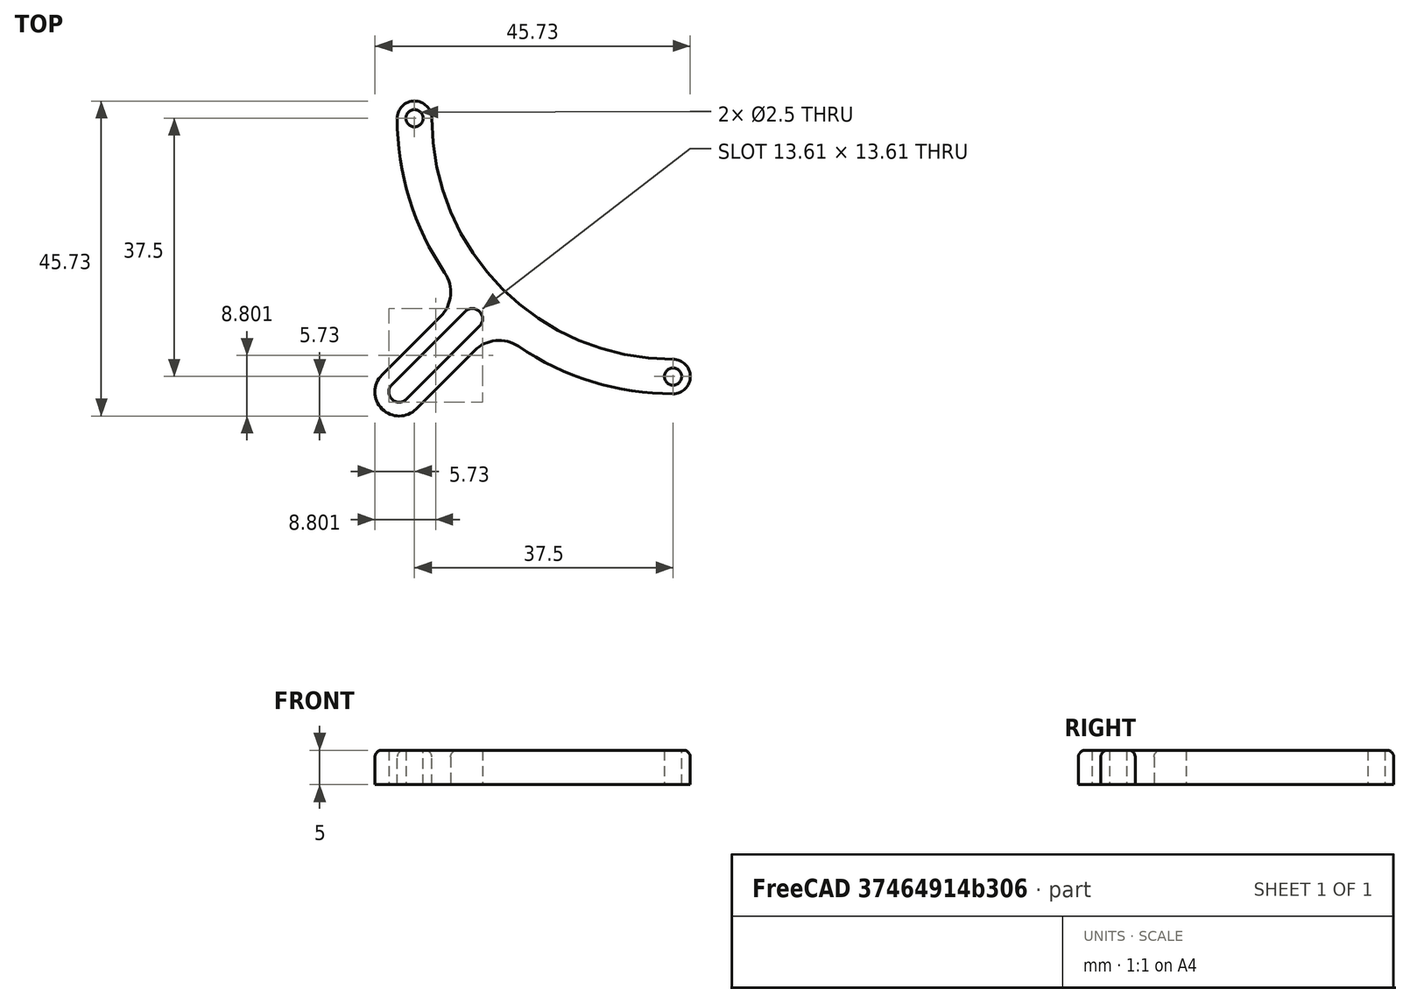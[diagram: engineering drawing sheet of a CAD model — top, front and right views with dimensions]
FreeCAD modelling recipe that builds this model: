
FCSTD DOCUMENT  (FreeCAD 2021.0205R23662 +3201 (Git))
Label: sketcher
License: All rights reserved
objects: Sketcher::SketchObject×1, PartDesign::Pad×1, PartDesign::Fillet×1, PartDesign::Body×1, App::Part×1, Mesh::Feature×1
note: 8 computed .brp shape members not serialized (recipe doc carries the construction recipe); baked Part::Feature solids carry a one-line shape summary decoded from their .brp

FEATURE [Sketcher::SketchObject] Sketch
  FullyConstrained = false
  MapMode = 5
  Support = -> [XY_Plane]
  sketch-geometry (17):
    g0: ArcOfCircle CenterX=0 CenterY=0 CenterZ=0 NormalX=0 NormalY=0 NormalZ=1 AngleXU=0 Radius=35 StartAngle=3.14159 EndAngle=4.71239
    g1: ArcOfCircle CenterX=0 CenterY=0 CenterZ=0 NormalX=0 NormalY=0 NormalZ=1 AngleXU=0 Radius=40 StartAngle=3.14159 EndAngle=3.73696
    g2: ArcOfCircle CenterX=-37.5 CenterY=0 CenterZ=0 NormalX=0 NormalY=0 NormalZ=1 AngleXU=0 Radius=2.5 StartAngle=0 EndAngle=3.14159
    g3: ArcOfCircle CenterX=0 CenterY=-37.5 CenterZ=0 NormalX=0 NormalY=0 NormalZ=1 AngleXU=0 Radius=2.5 StartAngle=4.71239 EndAngle=7.85398
    g4: Circle CenterX=-37.5 CenterY=0 CenterZ=0 NormalX=0 NormalY=0 NormalZ=1 AngleXU=0 Radius=1.25
    g5: Circle CenterX=0 CenterY=-37.5 CenterZ=0 NormalX=0 NormalY=0 NormalZ=1 AngleXU=0 Radius=1.25
    g6: LineSegment [constr] StartX=0 StartY=0 StartZ=0 EndX=-107.762 EndY=-107.762 EndZ=0
    g7: LineSegment StartX=-33.7219 StartY=-28.7721 StartZ=0 EndX=-42.2072 EndY=-37.2574 EndZ=0
    g8: ArcOfCircle CenterX=-39.7323 CenterY=-39.7323 CenterZ=0 NormalX=0 NormalY=0 NormalZ=1 AngleXU=0 Radius=3.5 StartAngle=2.35619 EndAngle=5.49779
    g9: LineSegment StartX=-37.2574 StartY=-42.2072 StartZ=0 EndX=-28.7721 EndY=-33.7219 EndZ=0
    g10: ArcOfCircle CenterX=0 CenterY=0 CenterZ=0 NormalX=0 NormalY=0 NormalZ=1 AngleXU=0 Radius=40 StartAngle=4.11702 EndAngle=4.71239
    g11: ArcOfCircle CenterX=-37.2574 CenterY=-25.2366 CenterZ=0 NormalX=0 NormalY=0 NormalZ=1 AngleXU=0 Radius=5 StartAngle=5.49779 EndAngle=6.87855
    g12: ArcOfCircle CenterX=-25.2366 CenterY=-37.2574 CenterZ=0 NormalX=0 NormalY=0 NormalZ=1 AngleXU=0 Radius=5 StartAngle=0.975429 EndAngle=2.35619
    g13: ArcOfCircle CenterX=-39.7323 CenterY=-39.7323 CenterZ=0 NormalX=0 NormalY=0 NormalZ=1 AngleXU=0 Radius=1.5 StartAngle=2.35619 EndAngle=5.49779
    g14: ArcOfCircle CenterX=-29.1257 CenterY=-29.1257 CenterZ=0 NormalX=0 NormalY=0 NormalZ=1 AngleXU=0 Radius=1.5 StartAngle=5.49779 EndAngle=8.63938
    g15: LineSegment StartX=-38.6716 StartY=-40.7929 StartZ=0 EndX=-28.065 EndY=-30.1863 EndZ=0
    g16: LineSegment StartX=-40.7929 StartY=-38.6716 StartZ=0 EndX=-30.1863 EndY=-28.065 EndZ=0
  constraints (44):
    c: Coincident(g0,g-1)
    c: PointOnObject(g0,g-1)
    c: PointOnObject(g0,g-2)
    c: Radius(g0) = 35
    c: Coincident(g1,g0)
    c: PointOnObject(g1,g-1)
    c: PointOnObject(g10,g-2)
    c: Radius(g1) = 40
    c: Coincident(g2,g1)
    c: Coincident(g2,g0)
    c: PointOnObject(g2,g-1)
    c: Coincident(g3,g0)
    c: Coincident(g3,g10)
    c: PointOnObject(g3,g-2)
    c: Coincident(g4,g2)
    c: Coincident(g5,g3)
    c: Equal(g4,g5)
    c: Diameter(g5) = 2.5
    c: Coincident(g6,g0)
    c: Angle(g-2,g6) = 2.35619
    c: Tangent(g7,g8) = -1.5708
    c: Tangent(g8,g9) = -1.5708
    c: Parallel(g7,g9)
    c: Parallel(g6,g9)
    c: Equal(g1,g10)
    c: Coincident(g1,g10)
    c: Tangent(g1,g11) = 1.5708
    c: Tangent(g7,g11) = 1.5708
    c: Tangent(g9,g12) = 1.5708
    c: Tangent(g10,g12) = 1.5708
    c: Equal(g11,g12)
    c: Radius(g11) = 5
    c: Diameter(g8) = 7
    c: PointOnObject(g8,g6)
    c: Distance(g8,g9) = 12
    c: Tangent(g13,g16) = 1.5708
    c: Tangent(g13,g15) = -1.5708
    c: Tangent(g15,g14) = -1.5708
    c: Tangent(g16,g14) = 1.5708
    c: Equal(g13,g14)
    c: Coincident(g13,g8)
    c: PointOnObject(g14,g6)
    c: Diameter(g14) = 3
    c: Distance(g15) = 15
FEATURE [PartDesign::Pad] Pad
  ClaimChildren = false
  Direction = (1,1,1)
  Fit = 0
  FitJoin = 0
  InnerFit = 0
  InnerFitJoin = 0
  InnerTaperAngle = 0
  InnerTaperAngleRev = 0
  Length = 5
  Length2 = 100
  NewSolid = false
  Profile = -> Sketch
  Suppress = false
  Type = 0
FEATURE [PartDesign::Fillet] Fillet
  Base = -> Pad [Edge22,Edge19,Edge16,Edge13,Edge10,Edge7,Edge4,Edge30,Edge28,Edge25]
  BaseFeature = -> Pad
  NewSolid = false
  Radius = 1
  SupportTransform = false
  Suppress = false
FEATURE [PartDesign::Body] Body
  AutoGroupSolids = false
  ExportMode = 0
  Group = -> [Sketch,Pad,Fillet]
  Origin = -> Origin001
  Tip = -> Fillet
  _ExportChildren = -> [Pad,Fillet]
  _GroupVersion = 1
FEATURE [App::Part] Part
  ExportMode = 1
  Group = -> [Body]
  Origin = -> Origin
  _ExportChildren = -> [Body]
  _GroupVersion = 1
FEATURE [Mesh::Feature] Mesh  label="Fillet (Meshed)"
